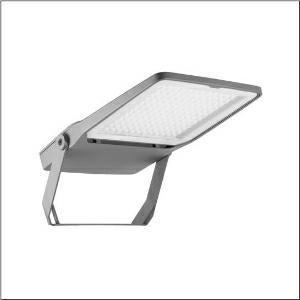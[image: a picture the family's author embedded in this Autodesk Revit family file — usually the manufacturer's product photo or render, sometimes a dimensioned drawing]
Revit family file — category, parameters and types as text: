
# Revit family: floodlight_fl_20_midi___pl43_5xa7682g2a1kc_f4ca
name_source: partatom
category: Lighting Fixtures
units: mm (PartAtom-declared; Revit-internal decimal feet)

## family parameters
Cut with Voids When Loaded = No
Host = Face
Light Source = No
Part Type = Normal
Room Calculation Point = No
Round Connector Dimension = Use Diameter
Shared = No

## types (1)
- --- (1 x LED 4000K / CRI = 70 (unbekannt), 38700 lm, 4000K)
    Apparent Load = 306 VA
    CIE Flux Codes = 32 74 99 100 100
    Color Rendering = 70
    Color Temperature = 4000K
    Default Elevation = 1800 mm
    Description = Floodlight FL 20 midi, floodlight, primary light control with lens, of plastic, primary optical cover: protective disc, of toughened safety glass, transparent, light distribution: PL43, light emission: direct distribution, primary light characteristic: asymmetric, installation type: surface-mounted, LED High Power LED, rated luminous flux: 38.700 lm, light colour: 740, colour temperature: 4000K, control gear: ECG Plus, control: overheat protection, power reduction, digital communication interface, flexible luminous flux parameterisation, time-dependent luminous flux control, electronic power reduction, with terminal, 10-pole, max. 2.5mm², mains connection: 220..240V, AC, 50/60Hz, rated input power: 306W, LED unit, of diecast aluminium, powder-coated, Siteco® metallic grey (DB 702S), length: 654 mm, width: 450 mm, height: 76mm, housing frame, of diecast aluminium, powder-coated, Siteco® metallic grey (DB 702S), DALIprotection rating (complete): IP66, insulation class (complete): insulation class II (safety insulation), certification: CE, ENEC, VDE, protection symbol: D, permissible ambient temperature for indoor applications: -40..+40°C, permissible ambient temperature for outdoor applications: -40..+50°C, standard: DIN EN 12944, packaging unit: 1 piece

Light Distribution: PL43
    Height = 76 mm
    Lamp = 1 x LED 4000K / CRI >= 70 (unbekannt)
    Lamp Light Flux = 38700 lm
    Lamp count = 1
    Length = 672 mm
    Luminous efficacy = 127 lm/W
    Manufacturer = Siteco
    ModVariant = No
    Model = 5XA7682G2A1KC
    Number of Poles = 1
    OnlyDefault = Yes
    Power Factor = 1
    Product Name = Floodlight FL 20 midi | PL43
    Product group = floodlight | pylon top
    ProductGroupID = 6101
    Protection Class = Protection class II
    Protection Degree = IP 66
    RLX_Detail_Level = 1
    RlxData = <blob elided: 97269 chars, md5=53730bf5>
    Socket = socket
    Standby Power = 0 W
    System Light Flux = 38700 lm
    System Power = 306 W
    Type Comments = factory setting: luminous flux: 100 % | dim-lin: 254 | 700 mA
    Type Image = l_1005943.jpg
    URL = http://relux.com
    VarID = @adj_143477
    Voltage = 0 V
    Weight = 0.00 kg
    Width = 450 mm

## geometry (parser evidence)
native form markers: Blend x4, Sweep x11
no freeform markers — native parametric forms only
